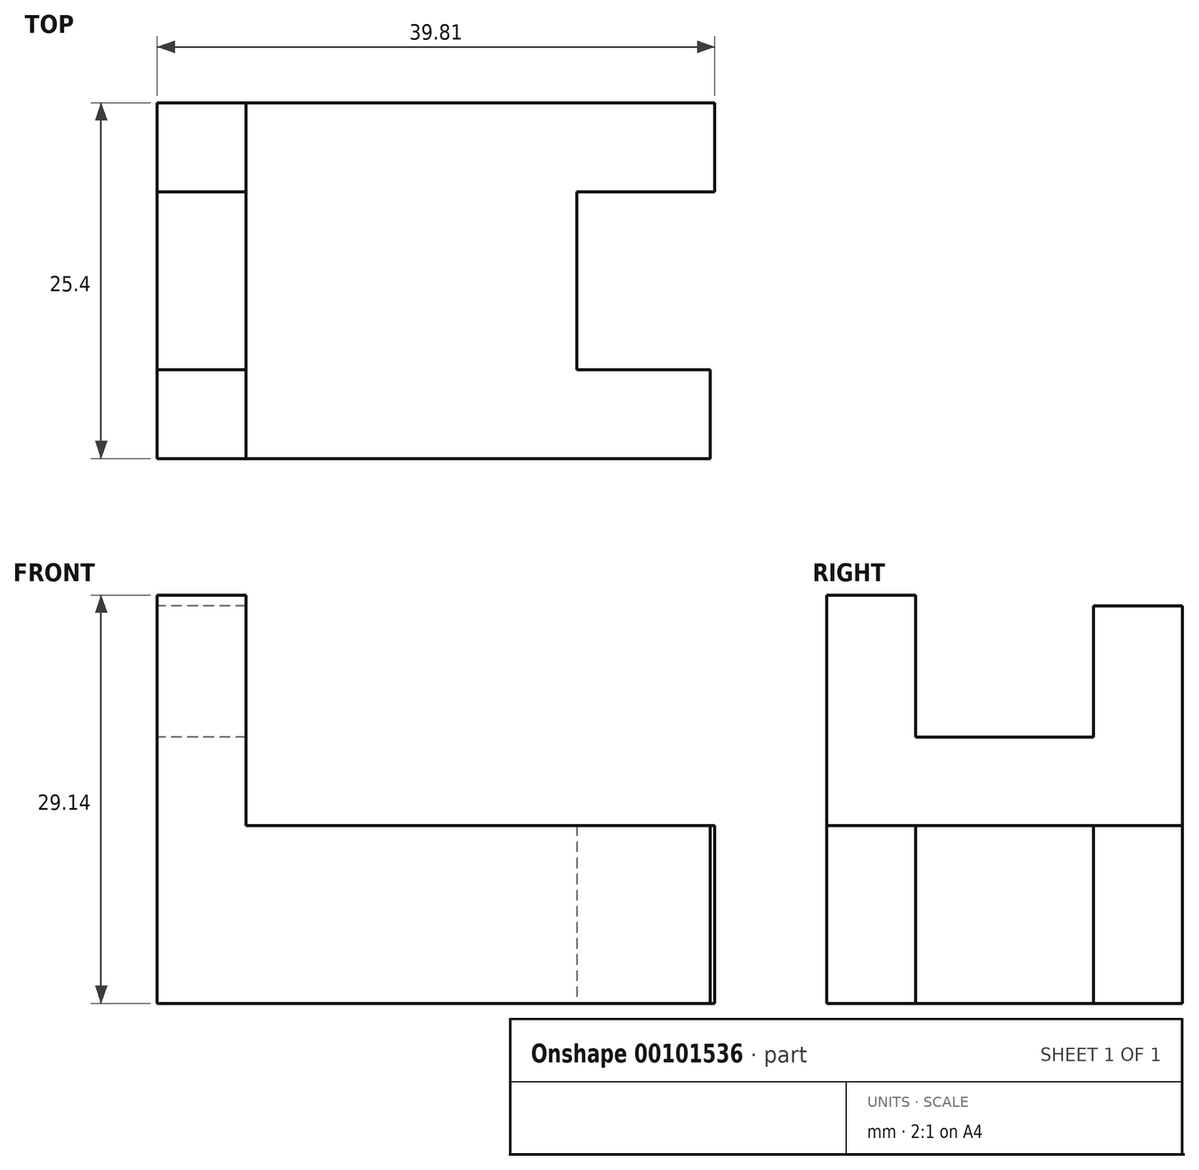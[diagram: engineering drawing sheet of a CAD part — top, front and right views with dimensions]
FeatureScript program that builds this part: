
annotation { "Feature Type Name" : "Feature", "Feature Type Description" : "" }
export const myFeature = defineFeature(function(context is Context, id is Id, definition is map)
    precondition{}
    {
        {
            var Q0;
            Q0=qCreatedBy(makeId("Top.planeOp"),FACE);
            var sketch = newSketch(context, id + "F0", { "sketchPlane" : qUnion([Q0])});
            skLineSegment(sketch, "E0", {"start": v(0, 25.4) * mm, "end": v(0, 0) * mm});
            skLineSegment(sketch, "E1", {"start": v(0, 0) * mm, "end": v(39.5, 0) * mm});
            skLineSegment(sketch, "E2", {"start": v(39.5, 0) * mm, "end": v(39.5, 6.35) * mm});
            skLineSegment(sketch, "E3", {"start": v(39.5, 6.35) * mm, "end": v(29.96, 6.35) * mm});
            skLineSegment(sketch, "E4", {"start": v(29.96, 6.35) * mm, "end": v(29.96, 19.05) * mm});
            skLineSegment(sketch, "E5", {"start": v(29.96, 19.05) * mm, "end": v(39.8, 19.05) * mm});
            skLineSegment(sketch, "E6", {"start": v(39.8, 19.05) * mm, "end": v(39.8, 25.4) * mm});
            skLineSegment(sketch, "E7", {"start": v(39.8, 25.4) * mm, "end": v(0, 25.4) * mm});
            skSolve(sketch);
        }
        {
            var Q0;
            Q0 = qSketchRegion(id + "F0", true);
            extrude(context, id + "F1", {"entities" : qUnion([Q0]), "depth" : 12.7 * mm});
        }
        {
            var Q0;
            Q0=makeQuery(id+"F1.opExtrude","SWEPT_FACE",FACE,{"disambiguationData":[OSD([sQuery(id+"F0.wireOp",EDGE,"E0")])]});
            var sketch = newSketch(context, id + "F2", { "sketchPlane" : qUnion([Q0])});
            skLineSegment(sketch, "E8", {"start": v(-25.4, 0) * mm, "end": v(-25.4, 28.36) * mm});
            skLineSegment(sketch, "E9", {"start": v(-25.4, 28.36) * mm, "end": v(-19.05, 28.36) * mm});
            skLineSegment(sketch, "E10", {"start": v(-19.05, 28.36) * mm, "end": v(-19.05, 19) * mm});
            skLineSegment(sketch, "E11", {"start": v(-19.05, 19) * mm, "end": v(-6.35, 19) * mm});
            skLineSegment(sketch, "E12", {"start": v(-6.35, 19) * mm, "end": v(-6.35, 29.14) * mm});
            skLineSegment(sketch, "E13", {"start": v(-6.35, 29.14) * mm, "end": v(0, 29.14) * mm});
            skLineSegment(sketch, "E14", {"start": v(0, 29.14) * mm, "end": v(0, 0) * mm});
            skSolve(sketch);
        }
        {
            var Q0;
            {var subQ1=sQuery(id+"F2.wireOp",EDGE,"E9");Q0=makeQuery(id+"F2.imprint","IMPRINT",FACE,{"disambiguationData":[TD([[makeQuery(id+"F2.imprint","IMPRINT",EDGE,{"derivedFrom":subQ1}),-1.0]])]});}
            extrude(context, id + "F3", {"entities" : qUnion([Q0]), "operationType" : NewBodyOperationType.ADD, "oppositeDirection" : true, "depth" : 6.35 * mm});
        }
    });
